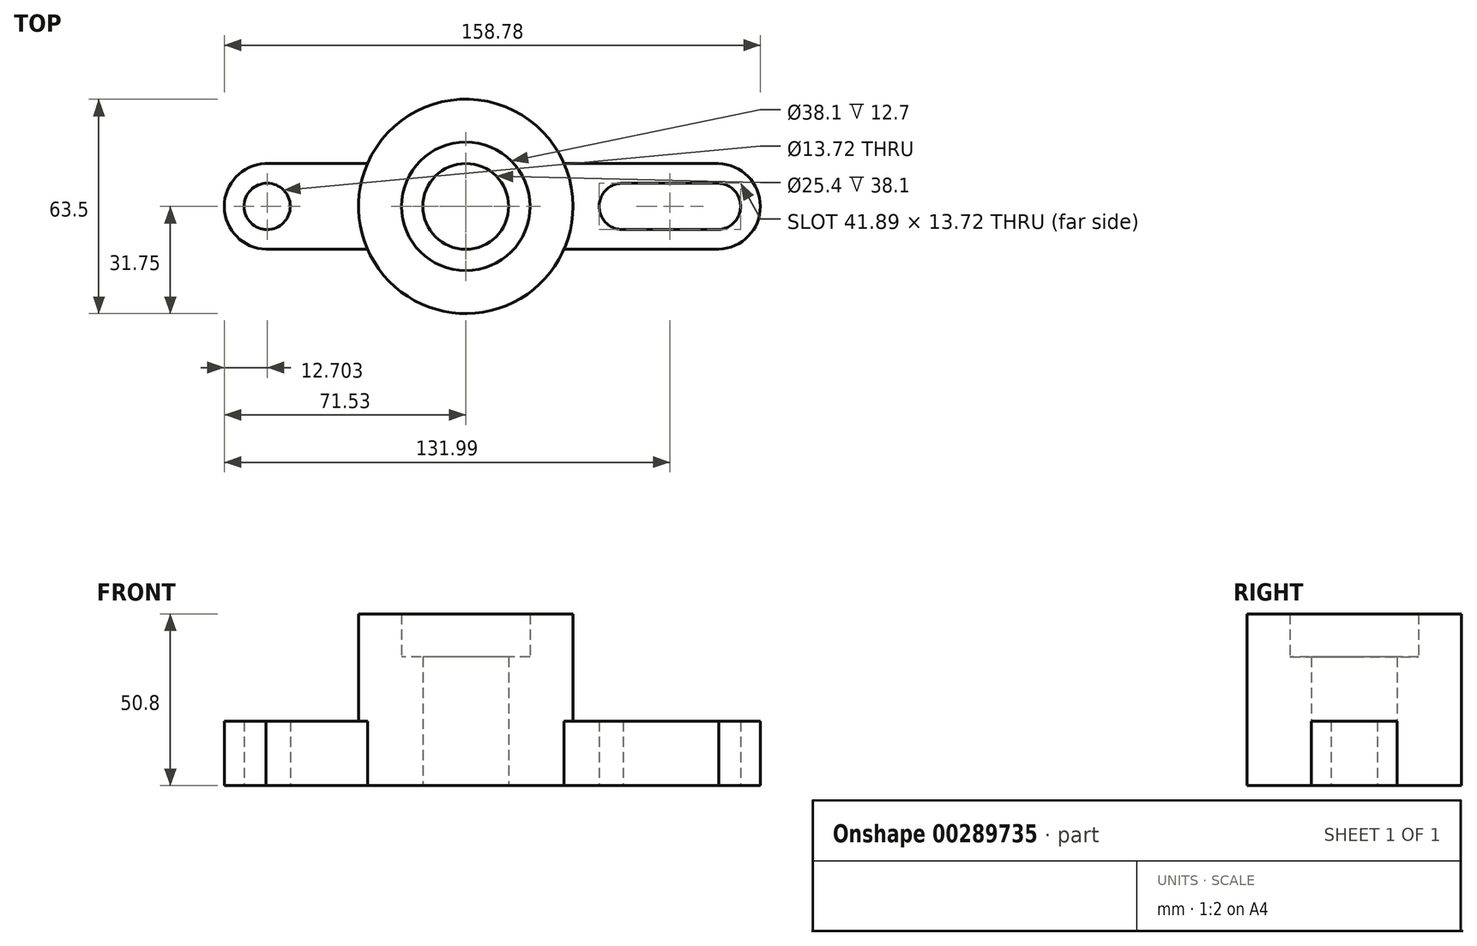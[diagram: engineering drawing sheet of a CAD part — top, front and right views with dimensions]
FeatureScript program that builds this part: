
annotation { "Feature Type Name" : "Feature", "Feature Type Description" : "" }
export const myFeature = defineFeature(function(context is Context, id is Id, definition is map)
    precondition{}
    {
        {
            var Q0;
            Q0=qCreatedBy(makeId("Top.planeOp"),FACE);
            var sketch = newSketch(context, id + "F0", { "sketchPlane" : qUnion([Q0])});
            skCircle(sketch, "E0", {"center": v(0, 0) * mm, "radius": 12.7 * mm});
            skCircle(sketch, "E1", {"center": v(0, 0) * mm, "radius": 19.05 * mm});
            skCircle(sketch, "E2", {"center": v(0, 0) * mm, "radius": 31.75 * mm});
            skPoint(sketch, "E3.start.orphan", {"position": v(0, 31.75) * mm});
            skArc(sketch, "E4", {"start": v(-58.25, 12.69) * mm, "mid": v(-71.53, 0.14) * mm, "end": v(-58.53, -12.7) * mm});
            skArc(sketch, "E5", {"start": v(74.12, -12.7) * mm, "mid": v(87.25, -0.06) * mm, "end": v(74.24, 12.7) * mm});
            skLineSegment(sketch, "E6", {"start": v(-59.4, 12.69) * mm, "end": v(-29.1, 12.69) * mm});
            skLineSegment(sketch, "E7", {"start": v(-59.13, -12.7) * mm, "end": v(-29.1, -12.7) * mm});
            skLineSegment(sketch, "E8", {"start": v(74.86, 12.7) * mm, "end": v(29.1, 12.7) * mm});
            skLineSegment(sketch, "E9", {"start": v(74.98, -12.7) * mm, "end": v(29.1, -12.7) * mm});
            skArc(sketch, "E10", {"start": v(74.55, -6.86) * mm, "mid": v(81.4, 0) * mm, "end": v(74.55, 6.86) * mm});
            skArc(sketch, "E11", {"start": v(46.4, 6.86) * mm, "mid": v(39.51, -0.1) * mm, "end": v(46.6, -6.85) * mm});
            skLineSegment(sketch, "E12", {"start": v(46.4, 6.86) * mm, "end": v(74.55, 6.86) * mm});
            skLineSegment(sketch, "E13", {"start": v(46.6, -6.85) * mm, "end": v(74.55, -6.86) * mm});
            skCircle(sketch, "E14", {"center": v(-58.83, 0) * mm, "radius": 6.86 * mm});
            skSolve(sketch);
        }
        {
            var Q0;
            Q0=makeQuery(id+"F0.imprint","IMPRINT",FACE,{"disambiguationData":[TD([[makeQuery(id+"F0.imprint","IMPRINT",EDGE,{"derivedFrom":sQuery(id+"F0.wireOp",EDGE,"E1")}),-1.0]])]});
            extrude(context, id + "F1", {"entities" : qUnion([Q0]), "depth" : 50.8 * mm});
        }
        {
            var Q0;
            Q0=makeQuery(id+"F0.imprint","IMPRINT",FACE,{"disambiguationData":[TD([[makeQuery(id+"F0.imprint","IMPRINT",EDGE,{"derivedFrom":sQuery(id+"F0.wireOp",EDGE,"E14")}),-1.0]])]});
            extrude(context, id + "F2", {"entities" : qUnion([Q0]), "operationType" : NewBodyOperationType.ADD, "depth" : 19.05 * mm});
        }
        {
            var Q0;
            Q0=makeQuery(id+"F0.imprint","IMPRINT",FACE,{"disambiguationData":[TD([[makeQuery(id+"F0.imprint","IMPRINT",EDGE,{"derivedFrom":sQuery(id+"F0.wireOp",EDGE,"E10")}),-1.0]])]});
            extrude(context, id + "F3", {"entities" : qUnion([Q0]), "operationType" : NewBodyOperationType.ADD, "depth" : 19.05 * mm});
        }
        {
            var Q0;
            Q0=makeQuery(id+"F0.imprint","IMPRINT",FACE,{"disambiguationData":[TD([[makeQuery(id+"F0.imprint","IMPRINT",EDGE,{"derivedFrom":sQuery(id+"F0.wireOp",EDGE,"E0")}),-1.0]])]});
            extrude(context, id + "F4", {"entities" : qUnion([Q0]), "operationType" : NewBodyOperationType.ADD, "depth" : 38.1 * mm});
        }
    });
